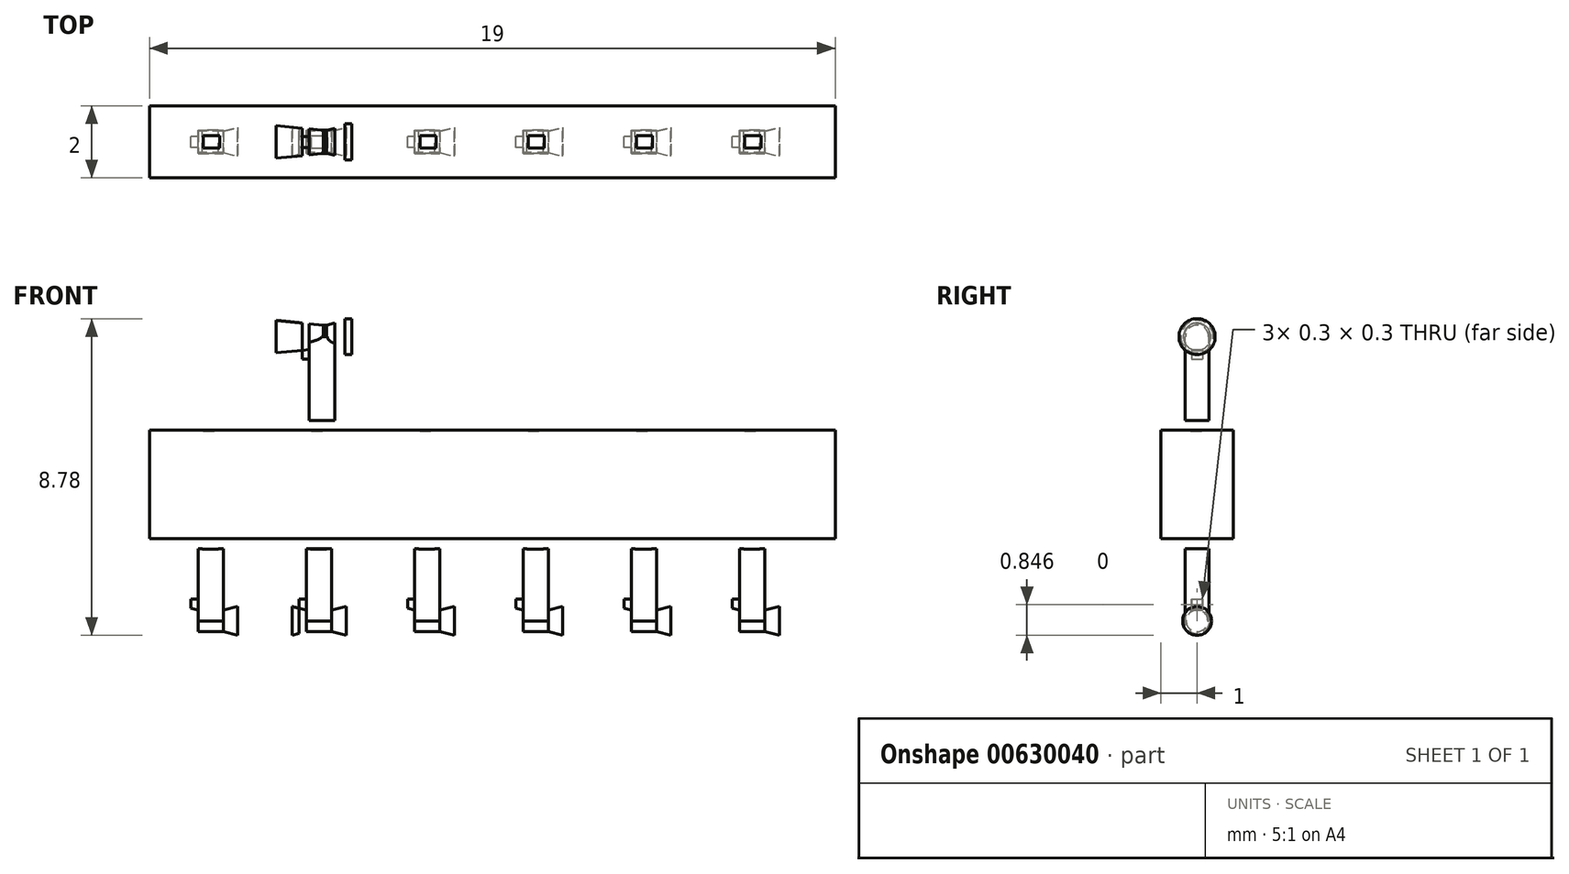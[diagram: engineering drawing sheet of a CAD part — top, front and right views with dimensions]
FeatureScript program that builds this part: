
annotation { "Feature Type Name" : "Feature", "Feature Type Description" : "" }
export const myFeature = defineFeature(function(context is Context, id is Id, definition is map)
    precondition{}
    {
        {
            var Q0;
            Q0=qCreatedBy(makeId("Front.planeOp"),FACE);
            var sketch = newSketch(context, id + "F0", { "sketchPlane" : qUnion([Q0])});
            skLineSegment(sketch, "E0.bottom", {"start": v(-0.48, 0) * mm, "end": v(0.22, 0) * mm});
            skLineSegment(sketch, "E0.top", {"start": v(-0.48, -2) * mm, "end": v(0.22, -2) * mm});
            skLineSegment(sketch, "E0.left", {"start": v(-0.48, 0) * mm, "end": v(-0.48, -2) * mm});
            skLineSegment(sketch, "E0.right", {"start": v(0.22, 0) * mm, "end": v(0.22, -2) * mm});
            skLineSegment(sketch, "E1.bottom", {"start": v(-0.48, 0) * mm, "end": v(-0.68, 0) * mm});
            skLineSegment(sketch, "E1.top", {"start": v(-0.48, -0.3) * mm, "end": v(-0.68, -0.3) * mm});
            skLineSegment(sketch, "E1.left", {"start": v(-0.48, 0) * mm, "end": v(-0.48, -0.3) * mm});
            skLineSegment(sketch, "E1.right", {"start": v(-0.68, 0) * mm, "end": v(-0.68, -0.3) * mm});
            skLineSegment(sketch, "E2", {"start": v(-0.1, 0) * mm, "end": v(-1.4, -0.13) * mm});
            skLineSegment(sketch, "E3", {"start": v(-1.4, -0.13) * mm, "end": v(-1.4, 0.32) * mm});
            skLineSegment(sketch, "E4", {"start": v(-1.4, 0.32) * mm, "end": v(0, 0.32) * mm});
            skLineSegment(sketch, "E5", {"start": v(0, 0.32) * mm, "end": v(0, 0) * mm});
            skLineSegment(sketch, "E6", {"start": v(0, 0) * mm, "end": v(0.5, -0.13) * mm});
            skLineSegment(sketch, "E7", {"start": v(0.5, -0.13) * mm, "end": v(0.5, 0.32) * mm});
            skLineSegment(sketch, "E8", {"start": v(0, 0.32) * mm, "end": v(0.5, 0.32) * mm});
            skLineSegment(sketch, "E9.bottom", {"start": v(0.5, 0.32) * mm, "end": v(0.7, 0.32) * mm});
            skLineSegment(sketch, "E9.top", {"start": v(0.5, -0.18) * mm, "end": v(0.7, -0.18) * mm});
            skLineSegment(sketch, "E9.left", {"start": v(0.5, 0.32) * mm, "end": v(0.5, -0.18) * mm});
            skLineSegment(sketch, "E9.right", {"start": v(0.7, 0.32) * mm, "end": v(0.7, -0.18) * mm});
            skLineSegment(sketch, "E10.bottom", {"start": v(-0.42, -2) * mm, "end": v(0.03, -2) * mm});
            skLineSegment(sketch, "E10.top", {"start": v(-0.42, -2.3) * mm, "end": v(0.03, -2.3) * mm});
            skLineSegment(sketch, "E10.left", {"start": v(-0.42, -2) * mm, "end": v(-0.42, -2.3) * mm});
            skLineSegment(sketch, "E10.right", {"start": v(0.03, -2) * mm, "end": v(0.03, -2.3) * mm});
            skLineSegment(sketch, "E11.top", {"start": v(-0.48, 0.32) * mm, "end": v(0.22, 0.32) * mm});
            skLineSegment(sketch, "E11.left", {"start": v(-0.48, 0) * mm, "end": v(-0.48, 0.32) * mm});
            skLineSegment(sketch, "E11.right", {"start": v(0.22, 0) * mm, "end": v(0.22, 0.32) * mm});
            skLineSegment(sketch, "E12.bottom", {"start": v(-0.68, 0) * mm, "end": v(-0.48, 0) * mm});
            skLineSegment(sketch, "E12.top", {"start": v(-0.68, 0.32) * mm, "end": v(-0.48, 0.32) * mm});
            skLineSegment(sketch, "E12.left", {"start": v(-0.68, 0) * mm, "end": v(-0.68, 0.32) * mm});
            skLineSegment(sketch, "E13.bottom", {"start": v(-4.9, -2.28) * mm, "end": v(14.1, -2.28) * mm});
            skLineSegment(sketch, "E13.top", {"start": v(-4.9, -5.28) * mm, "end": v(14.1, -5.28) * mm});
            skLineSegment(sketch, "E13.left", {"start": v(-4.9, -2.28) * mm, "end": v(-4.9, -5.28) * mm});
            skLineSegment(sketch, "E13.right", {"start": v(14.1, -2.28) * mm, "end": v(14.1, -5.28) * mm});
            skLineSegment(sketch, "E14.bottom", {"start": v(0, -5.28) * mm, "end": v(-0.45, -5.28) * mm});
            skLineSegment(sketch, "E14.top", {"start": v(0, -5.58) * mm, "end": v(-0.45, -5.58) * mm});
            skLineSegment(sketch, "E14.left", {"start": v(0, -5.28) * mm, "end": v(0, -5.58) * mm});
            skLineSegment(sketch, "E14.right", {"start": v(-0.45, -5.28) * mm, "end": v(-0.45, -5.58) * mm});
            skLineSegment(sketch, "E15.bottom", {"start": v(-0.56, -5.56) * mm, "end": v(0.14, -5.56) * mm});
            skLineSegment(sketch, "E15.top", {"start": v(-0.56, -7.56) * mm, "end": v(0.14, -7.56) * mm});
            skLineSegment(sketch, "E15.left", {"start": v(-0.56, -5.56) * mm, "end": v(-0.56, -7.56) * mm});
            skLineSegment(sketch, "E15.right", {"start": v(0.14, -5.56) * mm, "end": v(0.14, -7.56) * mm});
            skLineSegment(sketch, "E16", {"start": v(0.14, -7.56) * mm, "end": v(0.54, -7.56) * mm});
            skLineSegment(sketch, "E17", {"start": v(0.54, -7.56) * mm, "end": v(0.54, -7.16) * mm});
            skLineSegment(sketch, "E18", {"start": v(0.54, -7.16) * mm, "end": v(0.14, -7.26) * mm});
            skLineSegment(sketch, "E19", {"start": v(0.14, -7.26) * mm, "end": v(0.14, -7.56) * mm});
            skLineSegment(sketch, "E20", {"start": v(0.14, -7.26) * mm, "end": v(-0.56, -7.26) * mm});
            skLineSegment(sketch, "E21", {"start": v(-0.56, -7.26) * mm, "end": v(-0.96, -7.16) * mm});
            skLineSegment(sketch, "E22", {"start": v(-0.96, -7.56) * mm, "end": v(-0.96, -7.16) * mm});
            skLineSegment(sketch, "E23", {"start": v(-0.96, -7.56) * mm, "end": v(-0.56, -7.56) * mm});
            skLineSegment(sketch, "E24.bottom", {"start": v(-0.56, -7.56) * mm, "end": v(-0.76, -7.56) * mm});
            skLineSegment(sketch, "E24.top", {"start": v(-0.56, -6.96) * mm, "end": v(-0.76, -6.96) * mm});
            skLineSegment(sketch, "E24.left", {"start": v(-0.56, -7.56) * mm, "end": v(-0.56, -6.96) * mm});
            skLineSegment(sketch, "E24.right", {"start": v(-0.76, -7.56) * mm, "end": v(-0.76, -6.96) * mm});
            skSolve(sketch);
        }
        {
            var Q0;
            Q0=makeQuery(id+"F0.imprint","IMPRINT",FACE,{"disambiguationData":[TD([[makeQuery(id+"F0.imprint","IMPRINT",EDGE,{"derivedFrom":sQuery(id+"F0.wireOp",EDGE,"E12.bottom")}),1.0]])]});
            var Q1;
            {var subQ0=sQuery(id+"F0.wireOp",EDGE,"E12.bottom");Q1=makeQuery(id+"F0.imprint","IMPRINT",FACE,{"disambiguationData":[TD([[makeQuery(id+"F0.imprint","IMPRINT",EDGE,{"derivedFrom":subQ0}),-1.0]])]});}
            var Q2;
            {var subQ0=sQuery(id+"F0.wireOp",EDGE,"E0.bottom");var subQ3=sQuery(id+"F0.wireOp",EDGE,"E2");var subQ5=makeQuery(id+"F0.imprint","INTERSECT",VERTEX,{"derivedFrom":[subQ3,subQ0]});Q2=makeQuery(id+"F0.imprint","IMPRINT",FACE,{"disambiguationData":[TD([[makeQuery(id+"F0.imprint","IMPRINT",EDGE,{"disambiguationData":[TD([[subQ5,-1.0]])],"derivedFrom":subQ3}),-1.0]])]});}
            var Q3;
            {var subQ1=sQuery(id+"F0.wireOp",EDGE,"E5");Q3=makeQuery(id+"F0.imprint","IMPRINT",FACE,{"disambiguationData":[TD([[makeQuery(id+"F0.imprint","IMPRINT",EDGE,{"derivedFrom":subQ1}),-1.0]])]});}
            var Q4;
            {var subQ0=sQuery(id+"F0.wireOp",EDGE,"E5");Q4=makeQuery(id+"F0.imprint","IMPRINT",FACE,{"disambiguationData":[TD([[makeQuery(id+"F0.imprint","IMPRINT",EDGE,{"derivedFrom":subQ0}),1.0]])]});}
            var Q5;
            {var subQ1=sQuery(id+"F0.wireOp",EDGE,"E0.right");var subQ3=sQuery(id+"F0.wireOp",EDGE,"E6");var subQ4=makeQuery(id+"F0.imprint","INTERSECT",VERTEX,{"derivedFrom":[subQ1,subQ3]});Q5=makeQuery(id+"F0.imprint","IMPRINT",FACE,{"disambiguationData":[TD([[makeQuery(id+"F0.imprint","IMPRINT",EDGE,{"disambiguationData":[TD([[subQ4,1.0]])],"derivedFrom":subQ1}),-1.0]])]});}
            var Q6;
            {var subQ3=sQuery(id+"F0.wireOp",EDGE,"E9.bottom");Q6=makeQuery(id+"F0.imprint","IMPRINT",FACE,{"disambiguationData":[TD([[makeQuery(id+"F0.imprint","IMPRINT",EDGE,{"derivedFrom":subQ3}),-1.0]])]});}
            var Q7;
            {var subQ3=sQuery(id+"F0.wireOp",EDGE,"E8");Q7=makeQuery(id+"F0.imprint","IMPRINT",FACE,{"disambiguationData":[TD([[makeQuery(id+"F0.imprint","IMPRINT",EDGE,{"derivedFrom":subQ3}),-1.0]])]});}
            var Q8;
            {var subQ1=sQuery(id+"F0.wireOp",EDGE,"E3");Q8=makeQuery(id+"F0.imprint","IMPRINT",FACE,{"disambiguationData":[TD([[makeQuery(id+"F0.imprint","IMPRINT",EDGE,{"derivedFrom":subQ1}),-1.0]])]});}
            var Q9;
            Q9=sQuery(id+"F0.wireOp",EDGE,"E4");
            revolve(context, id + "F1", {"entities" : qUnion([Q0, Q1, Q2, Q3, Q4, Q5, Q6, Q7, Q8]), "axis" : qUnion([Q9]), "revolveType" : RevolveType.FULL});
        }
        {
            var Q0;
            {var subQ0=sQuery(id+"F0.wireOp",EDGE,"E1.top");Q0=makeQuery(id+"F0.imprint","IMPRINT",FACE,{"disambiguationData":[TD([[makeQuery(id+"F0.imprint","IMPRINT",EDGE,{"derivedFrom":subQ0}),-1.0]])]});}
            var Q1;
            Q1=makeQuery(id+"F0.imprint","IMPRINT",FACE,{"disambiguationData":[TD([[makeQuery(id+"F0.imprint","IMPRINT",EDGE,{"derivedFrom":sQuery(id+"F0.wireOp",EDGE,"E12.bottom")}),1.0]])]});
            var Q2;
            {var subQ0=sQuery(id+"F0.wireOp",EDGE,"E12.bottom");Q2=makeQuery(id+"F0.imprint","IMPRINT",FACE,{"disambiguationData":[TD([[makeQuery(id+"F0.imprint","IMPRINT",EDGE,{"derivedFrom":subQ0}),-1.0]])]});}
            extrude(context, id + "F2", {"entities" : qUnion([Q0, Q1, Q2]), "operationType" : NewBodyOperationType.ADD, "depth" : 0.3 * mm, "offsetDistance" : 25 * mm, "symmetric" : true});
        }
        {
            var Q0;
            {var subQ5=sQuery(id+"F0.wireOp",EDGE,"E0.left");Q0=makeQuery(id+"F0.imprint","IMPRINT",FACE,{"disambiguationData":[TD([[makeQuery(id+"F0.imprint","IMPRINT",EDGE,{"derivedFrom":subQ5}),1.0]])]});}
            var Q1;
            {var subQ0=sQuery(id+"F0.wireOp",EDGE,"E0.bottom");var subQ3=sQuery(id+"F0.wireOp",EDGE,"E2");var subQ5=makeQuery(id+"F0.imprint","INTERSECT",VERTEX,{"derivedFrom":[subQ3,subQ0]});Q1=makeQuery(id+"F0.imprint","IMPRINT",FACE,{"disambiguationData":[TD([[makeQuery(id+"F0.imprint","IMPRINT",EDGE,{"disambiguationData":[TD([[subQ5,-1.0]])],"derivedFrom":subQ3}),-1.0]])]});}
            var Q2;
            {var subQ1=sQuery(id+"F0.wireOp",EDGE,"E0.right");var subQ3=sQuery(id+"F0.wireOp",EDGE,"E6");var subQ4=makeQuery(id+"F0.imprint","INTERSECT",VERTEX,{"derivedFrom":[subQ1,subQ3]});Q2=makeQuery(id+"F0.imprint","IMPRINT",FACE,{"disambiguationData":[TD([[makeQuery(id+"F0.imprint","IMPRINT",EDGE,{"disambiguationData":[TD([[subQ4,1.0]])],"derivedFrom":subQ1}),-1.0]])]});}
            var Q3;
            {var subQ1=sQuery(id+"F0.wireOp",EDGE,"E5");Q3=makeQuery(id+"F0.imprint","IMPRINT",FACE,{"disambiguationData":[TD([[makeQuery(id+"F0.imprint","IMPRINT",EDGE,{"derivedFrom":subQ1}),-1.0]])]});}
            var Q4;
            {var subQ0=sQuery(id+"F0.wireOp",EDGE,"E5");Q4=makeQuery(id+"F0.imprint","IMPRINT",FACE,{"disambiguationData":[TD([[makeQuery(id+"F0.imprint","IMPRINT",EDGE,{"derivedFrom":subQ0}),1.0]])]});}
            extrude(context, id + "F3", {"entities" : qUnion([Q0, Q1, Q2, Q3, Q4]), "operationType" : NewBodyOperationType.ADD, "depth" : 0.65 * mm, "offsetDistance" : 25 * mm, "symmetric" : true});
        }
        {
            var Q0;
            Q0=makeQuery(id+"F0.imprint","IMPRINT",FACE,{"disambiguationData":[TD([[makeQuery(id+"F0.imprint","IMPRINT",EDGE,{"derivedFrom":sQuery(id+"F0.wireOp",EDGE,"E16")}),1.0]])]});
            var Q1;
            {var subQ5=sQuery(id+"F0.wireOp",EDGE,"E24.bottom");Q1=makeQuery(id+"F0.imprint","IMPRINT",FACE,{"disambiguationData":[TD([[makeQuery(id+"F0.imprint","IMPRINT",EDGE,{"derivedFrom":subQ5}),-1.0]])]});}
            var Q2;
            {var subQ0=sQuery(id+"F0.wireOp",EDGE,"E22");Q2=makeQuery(id+"F0.imprint","IMPRINT",FACE,{"disambiguationData":[TD([[makeQuery(id+"F0.imprint","IMPRINT",EDGE,{"derivedFrom":subQ0}),-1.0]])]});}
            var Q3;
            {var subQ0=sQuery(id+"F0.wireOp",EDGE,"E15.top");Q3=makeQuery(id+"F0.imprint","IMPRINT",FACE,{"disambiguationData":[TD([[makeQuery(id+"F0.imprint","IMPRINT",EDGE,{"derivedFrom":subQ0}),1.0]])]});}
            var Q4;
            Q4=sQuery(id+"F0.wireOp",EDGE,"E16");
            revolve(context, id + "F4", {"entities" : qUnion([Q0, Q1, Q2, Q3]), "axis" : qUnion([Q4]), "revolveType" : RevolveType.FULL});
        }
        {
            var Q0;
            {var subQ1=sQuery(id+"F0.wireOp",EDGE,"E14.top");Q0=makeQuery(id+"F0.imprint","IMPRINT",FACE,{"disambiguationData":[TD([[makeQuery(id+"F0.imprint","IMPRINT",EDGE,{"derivedFrom":subQ1}),1.0]])]});}
            var Q1;
            {var subQ0=sQuery(id+"F0.wireOp",EDGE,"E15.top");Q1=makeQuery(id+"F0.imprint","IMPRINT",FACE,{"disambiguationData":[TD([[makeQuery(id+"F0.imprint","IMPRINT",EDGE,{"derivedFrom":subQ0}),1.0]])]});}
            extrude(context, id + "F5", {"entities" : qUnion([Q0, Q1]), "operationType" : NewBodyOperationType.ADD, "depth" : 0.65 * mm, "offsetDistance" : 25 * mm, "symmetric" : true});
        }
        {
            var Q0;
            {var subQ5=sQuery(id+"F0.wireOp",EDGE,"E24.top");Q0=makeQuery(id+"F0.imprint","IMPRINT",FACE,{"disambiguationData":[TD([[makeQuery(id+"F0.imprint","IMPRINT",EDGE,{"derivedFrom":subQ5}),1.0]])]});}
            var Q1;
            {var subQ5=sQuery(id+"F0.wireOp",EDGE,"E24.bottom");Q1=makeQuery(id+"F0.imprint","IMPRINT",FACE,{"disambiguationData":[TD([[makeQuery(id+"F0.imprint","IMPRINT",EDGE,{"derivedFrom":subQ5}),-1.0]])]});}
            extrude(context, id + "F6", {"entities" : qUnion([Q0, Q1]), "operationType" : NewBodyOperationType.ADD, "depth" : 0.3 * mm, "offsetDistance" : 25 * mm, "symmetric" : true});
        }
        {
            var Q0;
            {var subQ0=sQuery(id+"F0.wireOp",EDGE,"E14.bottom");Q0=makeQuery(id+"F0.imprint","IMPRINT",FACE,{"disambiguationData":[TD([[makeQuery(id+"F0.imprint","IMPRINT",EDGE,{"derivedFrom":subQ0}),1.0]])]});}
            var Q1;
            {var subQ0=sQuery(id+"F0.wireOp",EDGE,"E14.top");Q1=makeQuery(id+"F0.imprint","IMPRINT",FACE,{"disambiguationData":[TD([[makeQuery(id+"F0.imprint","IMPRINT",EDGE,{"derivedFrom":subQ0}),-1.0]])]});}
            extrude(context, id + "F7", {"entities" : qUnion([Q0, Q1]), "depth" : 0.35 * mm, "offsetDistance" : 25 * mm, "symmetric" : true});
        }
        {
            var Q0;
            {var subQ0=sQuery(id+"F0.wireOp",EDGE,"E10.bottom");Q0=makeQuery(id+"F0.imprint","IMPRINT",FACE,{"disambiguationData":[TD([[makeQuery(id+"F0.imprint","IMPRINT",EDGE,{"derivedFrom":subQ0}),-1.0]])]});}
            var Q1;
            {var subQ0=sQuery(id+"F0.wireOp",EDGE,"E10.top");Q1=makeQuery(id+"F0.imprint","IMPRINT",FACE,{"disambiguationData":[TD([[makeQuery(id+"F0.imprint","IMPRINT",EDGE,{"derivedFrom":subQ0}),1.0]])]});}
            extrude(context, id + "F8", {"entities" : qUnion([Q0, Q1]), "depth" : 0.35 * mm, "offsetDistance" : 25 * mm, "symmetric" : true});
        }
        {
            var Q0;
            {var subQ1=sQuery(id+"F0.wireOp",EDGE,"E10.top");Q0=makeQuery(id+"F0.imprint","IMPRINT",FACE,{"disambiguationData":[TD([[makeQuery(id+"F0.imprint","IMPRINT",EDGE,{"derivedFrom":subQ1}),-1.0]])]});}
            var Q1;
            {var subQ0=sQuery(id+"F0.wireOp",EDGE,"E10.top");Q1=makeQuery(id+"F0.imprint","IMPRINT",FACE,{"disambiguationData":[TD([[makeQuery(id+"F0.imprint","IMPRINT",EDGE,{"derivedFrom":subQ0}),1.0]])]});}
            extrude(context, id + "F9", {"entities" : qUnion([Q0, Q1]), "depth" : 2 * mm, "offsetDistance" : 25 * mm, "symmetric" : true});
        }
        {
            var Q0;
            Q0=makeQuery(id+"F4.opRevolve","SWEPT_BODY",BODY,{"disambiguationData":[OSD([sQuery(id+"F0.wireOp",EDGE,"E15.top"),sQuery(id+"F0.wireOp",EDGE,"E16"),sQuery(id+"F0.wireOp",EDGE,"E17"),sQuery(id+"F0.wireOp",EDGE,"E18"),sQuery(id+"F0.wireOp",EDGE,"E20"),sQuery(id+"F0.wireOp",EDGE,"E21"),sQuery(id+"F0.wireOp",EDGE,"E22"),sQuery(id+"F0.wireOp",EDGE,"E23"),sQuery(id+"F0.wireOp",EDGE,"E24.bottom")])]});
            transform(context, id + "F10", {"entities" : qUnion([Q0]), "transformType" : TransformType.TRANSLATION_3D, "dx" : 3 * mm, "dy" : 0 * mm, "dz" : 0 * mm, "makeCopy" : true});
        }
        {
            var Q0;
            Q0=makeQuery(id+"F4.opRevolve","SWEPT_BODY",BODY,{"disambiguationData":[OSD([sQuery(id+"F0.wireOp",EDGE,"E15.top"),sQuery(id+"F0.wireOp",EDGE,"E16"),sQuery(id+"F0.wireOp",EDGE,"E17"),sQuery(id+"F0.wireOp",EDGE,"E18"),sQuery(id+"F0.wireOp",EDGE,"E20"),sQuery(id+"F0.wireOp",EDGE,"E21"),sQuery(id+"F0.wireOp",EDGE,"E22"),sQuery(id+"F0.wireOp",EDGE,"E23"),sQuery(id+"F0.wireOp",EDGE,"E24.bottom")])]});
            transform(context, id + "F11", {"entities" : qUnion([Q0]), "transformType" : TransformType.TRANSLATION_3D, "dx" : -3 * mm, "dy" : 0 * mm, "dz" : 0 * mm, "makeCopy" : true});
        }
        {
            var Q0;
            Q0=makeQuery(id+"F8.opExtrude","SWEPT_BODY",BODY,{"disambiguationData":[OSD([sQuery(id+"F0.wireOp",EDGE,"E10.bottom"),sQuery(id+"F0.wireOp",EDGE,"E10.top"),sQuery(id+"F0.wireOp",EDGE,"E10.left"),sQuery(id+"F0.wireOp",EDGE,"E10.right")])]});
            transform(context, id + "F12", {"entities" : qUnion([Q0]), "transformType" : TransformType.TRANSLATION_3D, "dx" : 3 * mm, "dy" : 0 * mm, "dz" : 0 * mm, "makeCopy" : true});
        }
        {
            var Q0;
            Q0=makeQuery(id+"F8.opExtrude","SWEPT_BODY",BODY,{"disambiguationData":[OSD([sQuery(id+"F0.wireOp",EDGE,"E10.bottom"),sQuery(id+"F0.wireOp",EDGE,"E10.top"),sQuery(id+"F0.wireOp",EDGE,"E10.left"),sQuery(id+"F0.wireOp",EDGE,"E10.right")])]});
            transform(context, id + "F13", {"entities" : qUnion([Q0]), "transformType" : TransformType.TRANSLATION_3D, "dx" : -3 * mm, "dy" : 0 * mm, "dz" : 0 * mm, "makeCopy" : true});
        }
        {
            var Q0;
            Q0=makeQuery(id+"F4.opRevolve","SWEPT_BODY",BODY,{"disambiguationData":[OSD([sQuery(id+"F0.wireOp",EDGE,"E15.top"),sQuery(id+"F0.wireOp",EDGE,"E16"),sQuery(id+"F0.wireOp",EDGE,"E17"),sQuery(id+"F0.wireOp",EDGE,"E18"),sQuery(id+"F0.wireOp",EDGE,"E20"),sQuery(id+"F0.wireOp",EDGE,"E21"),sQuery(id+"F0.wireOp",EDGE,"E22"),sQuery(id+"F0.wireOp",EDGE,"E23"),sQuery(id+"F0.wireOp",EDGE,"E24.bottom")])]});
            transform(context, id + "F14", {"entities" : qUnion([Q0]), "transformType" : TransformType.TRANSLATION_3D, "dx" : 6 * mm, "dy" : 0 * mm, "dz" : 0 * mm, "makeCopy" : true});
        }
        {
            var Q0;
            Q0=makeQuery(id+"F4.opRevolve","SWEPT_BODY",BODY,{"disambiguationData":[OSD([sQuery(id+"F0.wireOp",EDGE,"E15.top"),sQuery(id+"F0.wireOp",EDGE,"E16"),sQuery(id+"F0.wireOp",EDGE,"E17"),sQuery(id+"F0.wireOp",EDGE,"E18"),sQuery(id+"F0.wireOp",EDGE,"E20"),sQuery(id+"F0.wireOp",EDGE,"E21"),sQuery(id+"F0.wireOp",EDGE,"E22"),sQuery(id+"F0.wireOp",EDGE,"E23"),sQuery(id+"F0.wireOp",EDGE,"E24.bottom")])]});
            transform(context, id + "F15", {"entities" : qUnion([Q0]), "transformType" : TransformType.TRANSLATION_3D, "dx" : 9 * mm, "dy" : 0 * mm, "dz" : 0 * mm, "makeCopy" : true});
        }
        {
            var Q0;
            Q0=makeQuery(id+"F4.opRevolve","SWEPT_BODY",BODY,{"disambiguationData":[OSD([sQuery(id+"F0.wireOp",EDGE,"E15.top"),sQuery(id+"F0.wireOp",EDGE,"E16"),sQuery(id+"F0.wireOp",EDGE,"E17"),sQuery(id+"F0.wireOp",EDGE,"E18"),sQuery(id+"F0.wireOp",EDGE,"E20"),sQuery(id+"F0.wireOp",EDGE,"E21"),sQuery(id+"F0.wireOp",EDGE,"E22"),sQuery(id+"F0.wireOp",EDGE,"E23"),sQuery(id+"F0.wireOp",EDGE,"E24.bottom")])]});
            transform(context, id + "F16", {"entities" : qUnion([Q0]), "transformType" : TransformType.TRANSLATION_3D, "dx" : 12 * mm, "dy" : 0 * mm, "dz" : 0 * mm, "makeCopy" : true});
        }
        {
            var Q0;
            Q0=makeQuery(id+"F8.opExtrude","SWEPT_BODY",BODY,{"disambiguationData":[OSD([sQuery(id+"F0.wireOp",EDGE,"E10.bottom"),sQuery(id+"F0.wireOp",EDGE,"E10.top"),sQuery(id+"F0.wireOp",EDGE,"E10.left"),sQuery(id+"F0.wireOp",EDGE,"E10.right")])]});
            transform(context, id + "F17", {"entities" : qUnion([Q0]), "transformType" : TransformType.TRANSLATION_3D, "dx" : 6 * mm, "dy" : 0 * mm, "dz" : 0 * mm, "makeCopy" : true});
        }
        {
            var Q0;
            Q0=makeQuery(id+"F8.opExtrude","SWEPT_BODY",BODY,{"disambiguationData":[OSD([sQuery(id+"F0.wireOp",EDGE,"E10.bottom"),sQuery(id+"F0.wireOp",EDGE,"E10.top"),sQuery(id+"F0.wireOp",EDGE,"E10.left"),sQuery(id+"F0.wireOp",EDGE,"E10.right")])]});
            transform(context, id + "F18", {"entities" : qUnion([Q0]), "transformType" : TransformType.TRANSLATION_3D, "dx" : 12 * mm, "dy" : 0 * mm, "dz" : 0 * mm, "makeCopy" : true});
        }
        {
            var Q0;
            Q0=makeQuery(id+"F8.opExtrude","SWEPT_BODY",BODY,{"disambiguationData":[OSD([sQuery(id+"F0.wireOp",EDGE,"E10.bottom"),sQuery(id+"F0.wireOp",EDGE,"E10.top"),sQuery(id+"F0.wireOp",EDGE,"E10.left"),sQuery(id+"F0.wireOp",EDGE,"E10.right")])]});
            transform(context, id + "F19", {"entities" : qUnion([Q0]), "transformType" : TransformType.TRANSLATION_3D, "dx" : 9 * mm, "dy" : 0 * mm, "dz" : 0 * mm, "makeCopy" : true});
        }
    });
